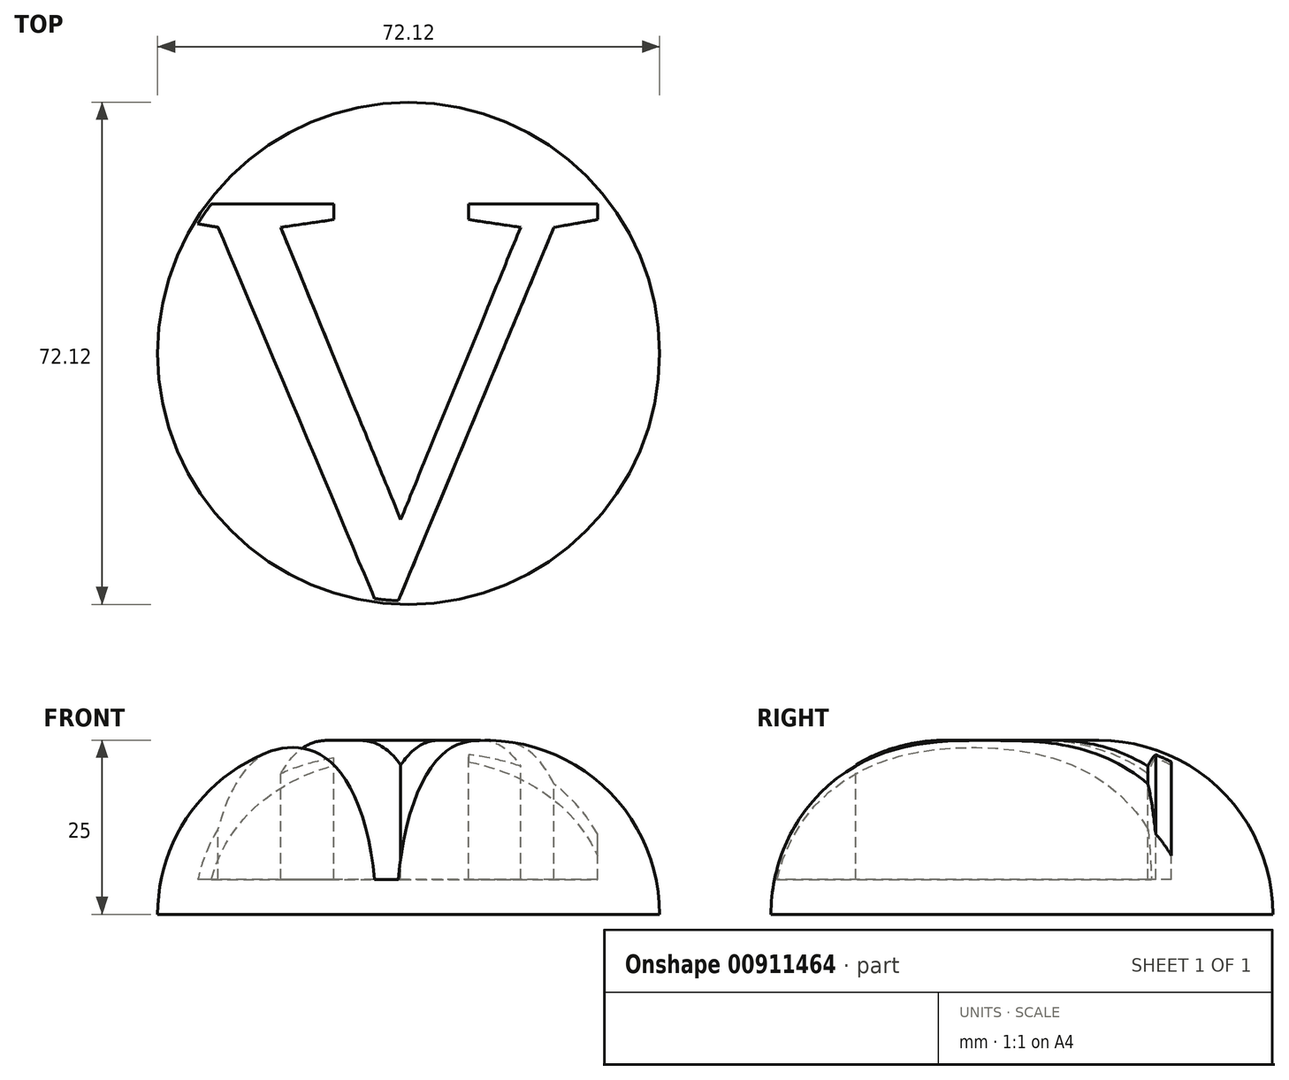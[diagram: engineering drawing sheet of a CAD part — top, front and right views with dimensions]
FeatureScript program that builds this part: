
annotation { "Feature Type Name" : "Feature", "Feature Type Description" : "" }
export const myFeature = defineFeature(function(context is Context, id is Id, definition is map)
    precondition{}
    {
        {
            var Q0;
            Q0=qCreatedBy(makeId("Top.planeOp"),FACE);
            var sketch = newSketch(context, id + "F0", { "sketchPlane" : qUnion([Q0])});
            skCircle(sketch, "E0", {"center": v(0, 0) * mm, "radius": 36.06 * mm});
            skSolve(sketch);
        }
        {
            var Q0;
            Q0=makeQuery(id+"F0.imprint","IMPRINT",FACE,{"disambiguationData":[TD([[makeQuery(id+"F0.imprint","IMPRINT",EDGE,{"derivedFrom":sQuery(id+"F0.wireOp",EDGE,"E0")}),1.0]])]});
            extrude(context, id + "F1", {"entities" : qUnion([Q0]), "depth" : 25 * mm, "offsetDistance" : 25 * mm});
        }
        {
            var Q0;
            Q0=makeQuery(id+"F1.opExtrude","CAP_FACE",FACE,{"disambiguationData":[OSD([sQuery(id+"F0.wireOp",EDGE,"E0")])],"isStart":false});
            fillet(context, id + "F2", {"entities" : qUnion([Q0]), "radius" : 25 * mm, "tangentPropagation" : true, "allowEdgeOverflow" : false});
        }
        {
            var Q0;
            Q0=makeQuery(id+"F1.opExtrude","CAP_FACE",FACE,{"disambiguationData":[OSD([sQuery(id+"F0.wireOp",EDGE,"E0")])],"isStart":false});
            var sketch = newSketch(context, id + "F3", { "sketchPlane" : qUnion([Q0])});
            skText(sketch, "E1", { "text": "V", "fontName": "Tinos-Regular.ttf"});
            const initialGuessF3  = {"E1": [-0.03477, -0.03555, 1, 0, 0.06269]};
            skSetInitialGuess(sketch, initialGuessF3);
            skSolve(sketch);
        }
        {
            var Q0;
            Q0 = qSketchRegion(id + "F3", true);
            extrude(context, id + "F4", {"entities" : qUnion([Q0]), "operationType" : NewBodyOperationType.REMOVE, "oppositeDirection" : true, "depth" : 20 * mm, "offsetDistance" : 25 * mm});
        }
    });
